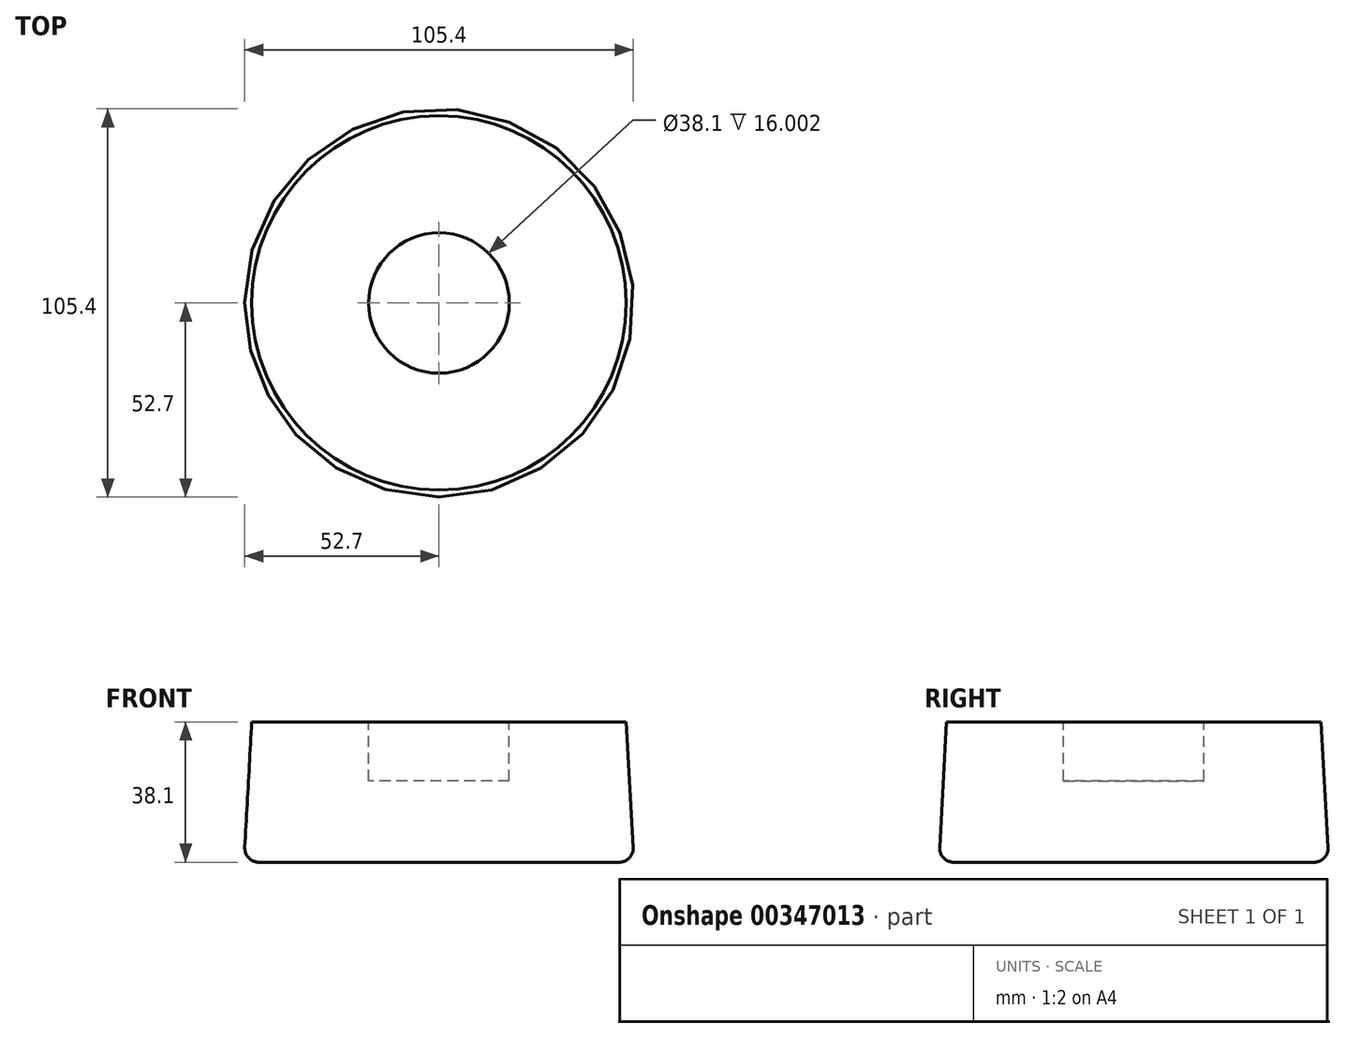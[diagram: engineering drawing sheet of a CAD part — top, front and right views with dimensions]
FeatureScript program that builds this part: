
annotation { "Feature Type Name" : "Feature", "Feature Type Description" : "" }
export const myFeature = defineFeature(function(context is Context, id is Id, definition is map)
    precondition{}
    {
        {
            var Q0;
            Q0=qCreatedBy(makeId("Front.planeOp"),FACE);
            var sketch = newSketch(context, id + "F0", { "sketchPlane" : qUnion([Q0])});
            skLineSegment(sketch, "E0", {"start": v(0, 13.77) * mm, "end": v(-50.8, 13.77) * mm});
            skLineSegment(sketch, "E1", {"start": v(-50.8, 13.77) * mm, "end": v(-52.7, -20.3) * mm});
            skLineSegment(sketch, "E2", {"start": v(-48.89, -24.33) * mm, "end": v(0, -24.33) * mm});
            skLineSegment(sketch, "E3", {"start": v(0, -24.33) * mm, "end": v(0, 13.77) * mm});
            skPoint(sketch, "E4.visualSharp", {"position": v(-52.92, -24.33) * mm});
            skArc(sketch, "E4.filletArc", {"start": v(-52.7, -20.3) * mm, "mid": v(-51.66, -23.13) * mm, "end": v(-48.89, -24.33) * mm});
            skSolve(sketch);
        }
        {
            var Q0;
            Q0=makeQuery(id+"F0.imprint","IMPRINT",FACE,{"disambiguationData":[TD([[makeQuery(id+"F0.imprint","IMPRINT",EDGE,{"derivedFrom":sQuery(id+"F0.wireOp",EDGE,"E0")}),1.0]])]});
            var Q1;
            Q1=sQuery(id+"F0.wireOp",EDGE,"E3");
            revolve(context, id + "F1", {"entities" : qUnion([Q0]), "axis" : qUnion([Q1]), "revolveType" : RevolveType.FULL});
        }
        {
            var Q0;
            Q0=makeQuery(id+"F1.opRevolve","SWEPT_FACE",FACE,{"disambiguationData":[OSD([sQuery(id+"F0.wireOp",EDGE,"E0")])]});
            var sketch = newSketch(context, id + "F2", { "sketchPlane" : qUnion([Q0])});
            skCircle(sketch, "E5", {"center": v(0, 0) * mm, "radius": 19.05 * mm});
            skSolve(sketch);
        }
        {
            var Q0;
            Q0=makeQuery(id+"F2.imprint","IMPRINT",FACE,{"disambiguationData":[TD([[makeQuery(id+"F2.imprint","IMPRINT",EDGE,{"derivedFrom":sQuery(id+"F2.wireOp",EDGE,"E5")}),1.0]])]});
            extrude(context, id + "F3", {"entities" : qUnion([Q0]), "operationType" : NewBodyOperationType.REMOVE, "oppositeDirection" : true, "depth" : 16 * mm});
        }
    });
